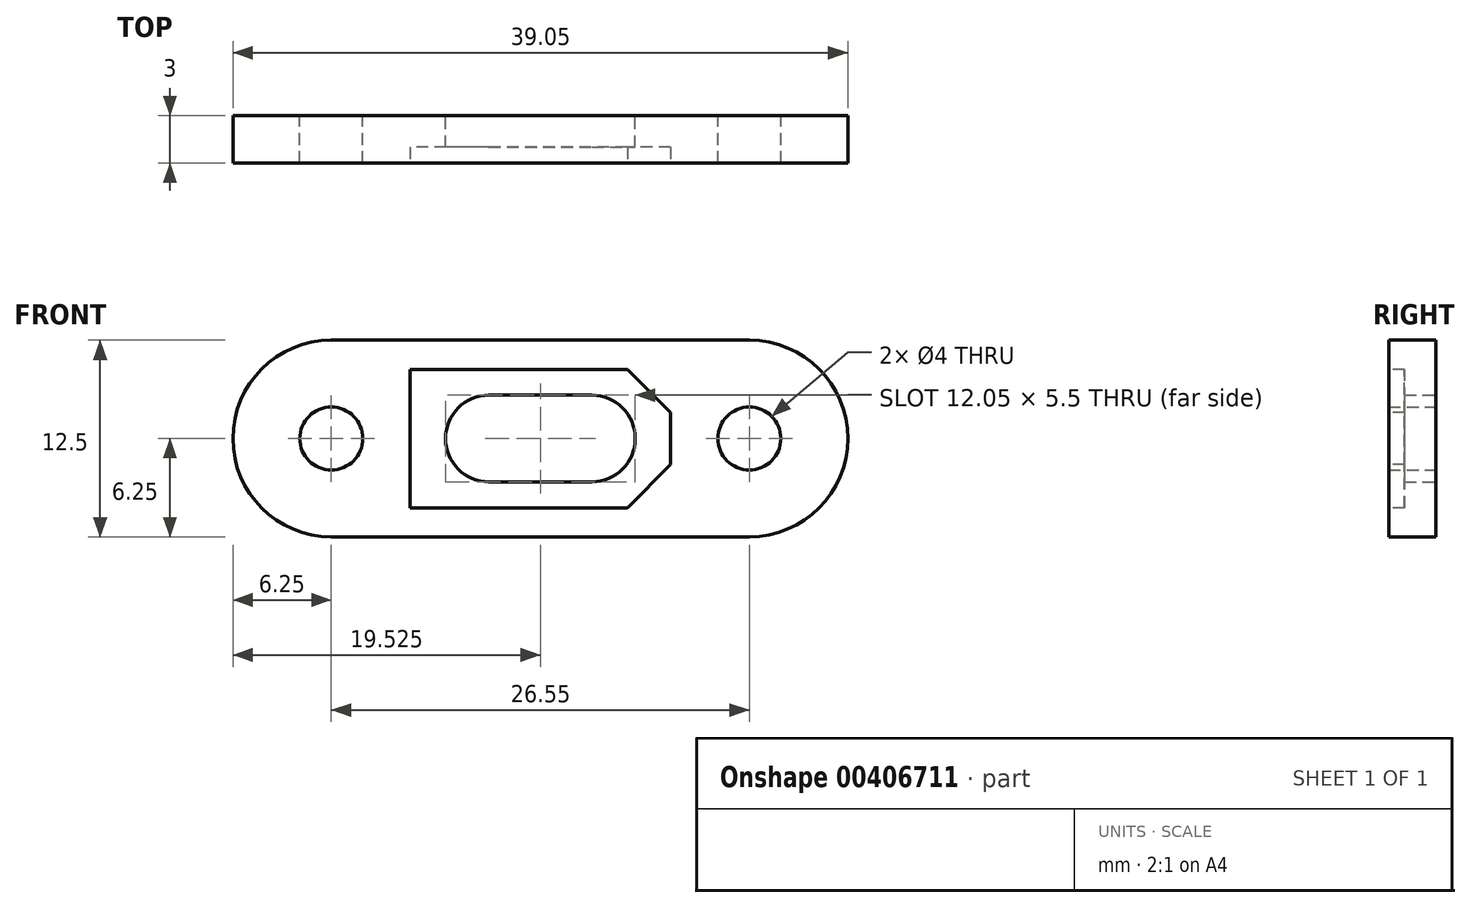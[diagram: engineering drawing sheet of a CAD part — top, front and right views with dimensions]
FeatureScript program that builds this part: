
annotation { "Feature Type Name" : "Feature", "Feature Type Description" : "" }
export const myFeature = defineFeature(function(context is Context, id is Id, definition is map)
    precondition{}
    {
        {
            var Q0;
            Q0=qCreatedBy(makeId("Front.planeOp"),FACE);
            var sketch = newSketch(context, id + "F0", { "sketchPlane" : qUnion([Q0])});
            skLineSegment(sketch, "E0.bottom", {"start": v(0, 12.5) * mm, "end": v(26.55, 12.5) * mm});
            skLineSegment(sketch, "E0.top", {"start": v(0, 0) * mm, "end": v(26.55, 0) * mm});
            skCircle(sketch, "E1", {"center": v(0, 6.25) * mm, "radius": 2 * mm});
            skCircle(sketch, "E2", {"center": v(26.55, 6.25) * mm, "radius": 2 * mm});
            skArc(sketch, "E3", {"start": v(0, 12.5) * mm, "mid": v(-6.25, 6.25) * mm, "end": v(0, 0) * mm});
            skArc(sketch, "E4", {"start": v(26.55, 0) * mm, "mid": v(32.8, 6.25) * mm, "end": v(26.55, 12.5) * mm});
            skLineSegment(sketch, "E5.bottom", {"start": v(10, 9) * mm, "end": v(16.55, 9) * mm});
            skLineSegment(sketch, "E5.top", {"start": v(10, 3.5) * mm, "end": v(16.55, 3.5) * mm});
            skArc(sketch, "E6", {"start": v(10, 9) * mm, "mid": v(7.25, 6.25) * mm, "end": v(10, 3.5) * mm});
            skArc(sketch, "E7", {"start": v(16.55, 3.5) * mm, "mid": v(19.3, 6.25) * mm, "end": v(16.55, 9) * mm});
            skSolve(sketch);
        }
        {
            var Q0;
            Q0=makeQuery(id+"F0.imprint","IMPRINT",FACE,{"disambiguationData":[TD([[makeQuery(id+"F0.imprint","IMPRINT",EDGE,{"derivedFrom":sQuery(id+"F0.wireOp",EDGE,"E0.bottom")}),-1.0]])]});
            extrude(context, id + "F1", {"entities" : qUnion([Q0]), "depth" : 3 * mm});
        }
        {
            var Q0;
            Q0=makeQuery(id+"F1.opExtrude","CAP_FACE",FACE,{"disambiguationData":[OSD([sQuery(id+"F0.wireOp",EDGE,"E0.bottom"),sQuery(id+"F0.wireOp",EDGE,"E0.top"),sQuery(id+"F0.wireOp",EDGE,"E1"),sQuery(id+"F0.wireOp",EDGE,"E2"),sQuery(id+"F0.wireOp",EDGE,"E3"),sQuery(id+"F0.wireOp",EDGE,"E4"),sQuery(id+"F0.wireOp",EDGE,"E5.bottom"),sQuery(id+"F0.wireOp",EDGE,"E5.top"),sQuery(id+"F0.wireOp",EDGE,"E6"),sQuery(id+"F0.wireOp",EDGE,"E7")])],"isStart":false});
            var sketch = newSketch(context, id + "F2", { "sketchPlane" : qUnion([Q0])});
            skLineSegment(sketch, "E8.0", {"start": v(21.55, 7.9) * mm, "end": v(18.8, 10.65) * mm});
            skLineSegment(sketch, "E8.1", {"start": v(5, 10.65) * mm, "end": v(5, 1.85) * mm});
            skLineSegment(sketch, "E8.2", {"start": v(5, 1.85) * mm, "end": v(18.8, 1.85) * mm});
            skLineSegment(sketch, "E8.3", {"start": v(18.8, 10.65) * mm, "end": v(5, 10.65) * mm});
            skLineSegment(sketch, "E8.4", {"start": v(18.8, 1.85) * mm, "end": v(21.55, 4.6) * mm});
            skLineSegment(sketch, "E8.5", {"start": v(21.55, 4.6) * mm, "end": v(21.55, 7.9) * mm});
            skSolve(sketch);
        }
        {
            var Q0;
            Q0=makeQuery(id+"F2.imprint","IMPRINT",FACE,{"disambiguationData":[TD([[makeQuery(id+"F2.imprint","IMPRINT",EDGE,{"derivedFrom":sQuery(id+"F2.wireOp",EDGE,"E8.0")}),1.0]])]});
            extrude(context, id + "F3", {"entities" : qUnion([Q0]), "operationType" : NewBodyOperationType.REMOVE, "oppositeDirection" : true, "depth" : 1 * mm});
        }
    });
